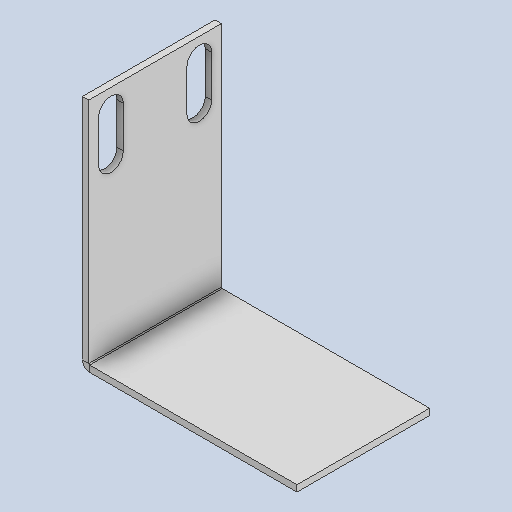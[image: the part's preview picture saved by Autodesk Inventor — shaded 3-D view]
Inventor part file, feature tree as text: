
AUTODESK INVENTOR PART (.ipt)
format: ipt  version: 2022 (Build 260153000, 153)  size: 95,744 bytes
history: native  units: in
note: dims shown in document units (in); Inventor stores cm internally (conversion verified against a paired STEP export)
features: sketch x1
ambient origin geometry x8: Origin, YZ Plane, XZ Plane, XY Plane, X Axis, Y Axis, Z Axis, Center Point
bodies: Solid1 (feature_tree)
feature tree (1):
  sketch  "Sketched Bend1"
